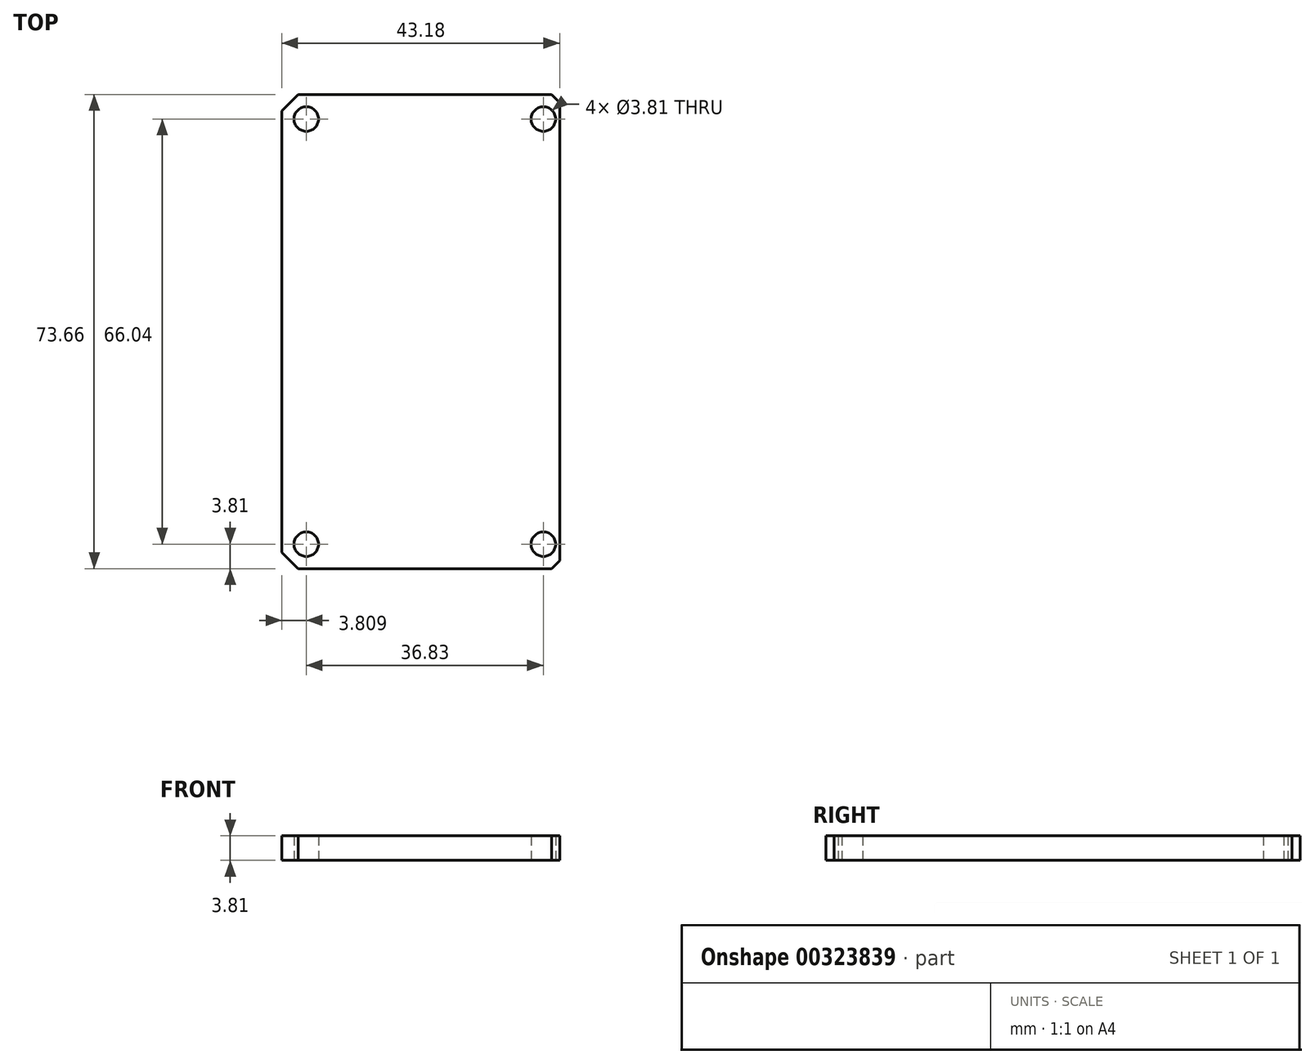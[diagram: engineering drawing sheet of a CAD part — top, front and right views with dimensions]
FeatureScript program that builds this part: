
annotation { "Feature Type Name" : "Feature", "Feature Type Description" : "" }
export const myFeature = defineFeature(function(context is Context, id is Id, definition is map)
    precondition{}
    {
        {
            var Q0;
            Q0=qCreatedBy(makeId("Top.planeOp"),FACE);
            var sketch = newSketch(context, id + "F0", { "sketchPlane" : qUnion([Q0])});
            skLineSegment(sketch, "E0.bottom", {"start": v(-80.1, 87.1) * mm, "end": v(-36.91, 87.1) * mm});
            skLineSegment(sketch, "E0.top", {"start": v(-80.1, 13.44) * mm, "end": v(-36.91, 13.44) * mm});
            skLineSegment(sketch, "E0.left", {"start": v(-80.1, 87.1) * mm, "end": v(-80.1, 13.44) * mm});
            skLineSegment(sketch, "E0.right", {"start": v(-36.91, 87.1) * mm, "end": v(-36.91, 13.44) * mm});
            skCircle(sketch, "E1", {"center": v(-76.28, 83.29) * mm, "radius": 1.9 * mm});
            skCircle(sketch, "E2", {"center": v(-39.45, 83.29) * mm, "radius": 1.9 * mm});
            skCircle(sketch, "E3", {"center": v(-39.45, 17.25) * mm, "radius": 1.9 * mm});
            skCircle(sketch, "E4", {"center": v(-76.28, 17.25) * mm, "radius": 1.9 * mm});
            skSolve(sketch);
        }
        {
            var Q0;
            Q0=makeQuery(id+"F0.imprint","IMPRINT",FACE,{"disambiguationData":[TD([[makeQuery(id+"F0.imprint","IMPRINT",EDGE,{"derivedFrom":sQuery(id+"F0.wireOp",EDGE,"E0.bottom")}),-1.0]])]});
            extrude(context, id + "F1", {"entities" : qUnion([Q0]), "depth" : 3.8 * mm});
        }
        {
            var Q0;
            Q0=makeQuery(id+"F1.opExtrude","SWEPT_EDGE",EDGE,{"disambiguationData":[OSD([sQuery(id+"F0.wireOp",EDGE,"E0.top"),sQuery(id+"F0.wireOp",EDGE,"E0.right")])]});
            var Q1;
            Q1=makeQuery(id+"F1.opExtrude","SWEPT_EDGE",EDGE,{"disambiguationData":[OSD([sQuery(id+"F0.wireOp",EDGE,"E0.bottom"),sQuery(id+"F0.wireOp",EDGE,"E0.right")])]});
            chamfer(context, id + "F2", {"entities" : qUnion([Q0, Q1]), "width" : 1.27 * mm, "tangentPropagation" : true});
        }
        {
            var Q0;
            Q0=makeQuery(id+"F1.opExtrude","SWEPT_EDGE",EDGE,{"disambiguationData":[OSD([sQuery(id+"F0.wireOp",EDGE,"E0.top"),sQuery(id+"F0.wireOp",EDGE,"E0.left")])]});
            var Q1;
            Q1=makeQuery(id+"F1.opExtrude","SWEPT_EDGE",EDGE,{"disambiguationData":[OSD([sQuery(id+"F0.wireOp",EDGE,"E0.bottom"),sQuery(id+"F0.wireOp",EDGE,"E0.left")])]});
            chamfer(context, id + "F3", {"entities" : qUnion([Q0, Q1]), "width" : 2.54 * mm, "tangentPropagation" : true});
        }
    });
